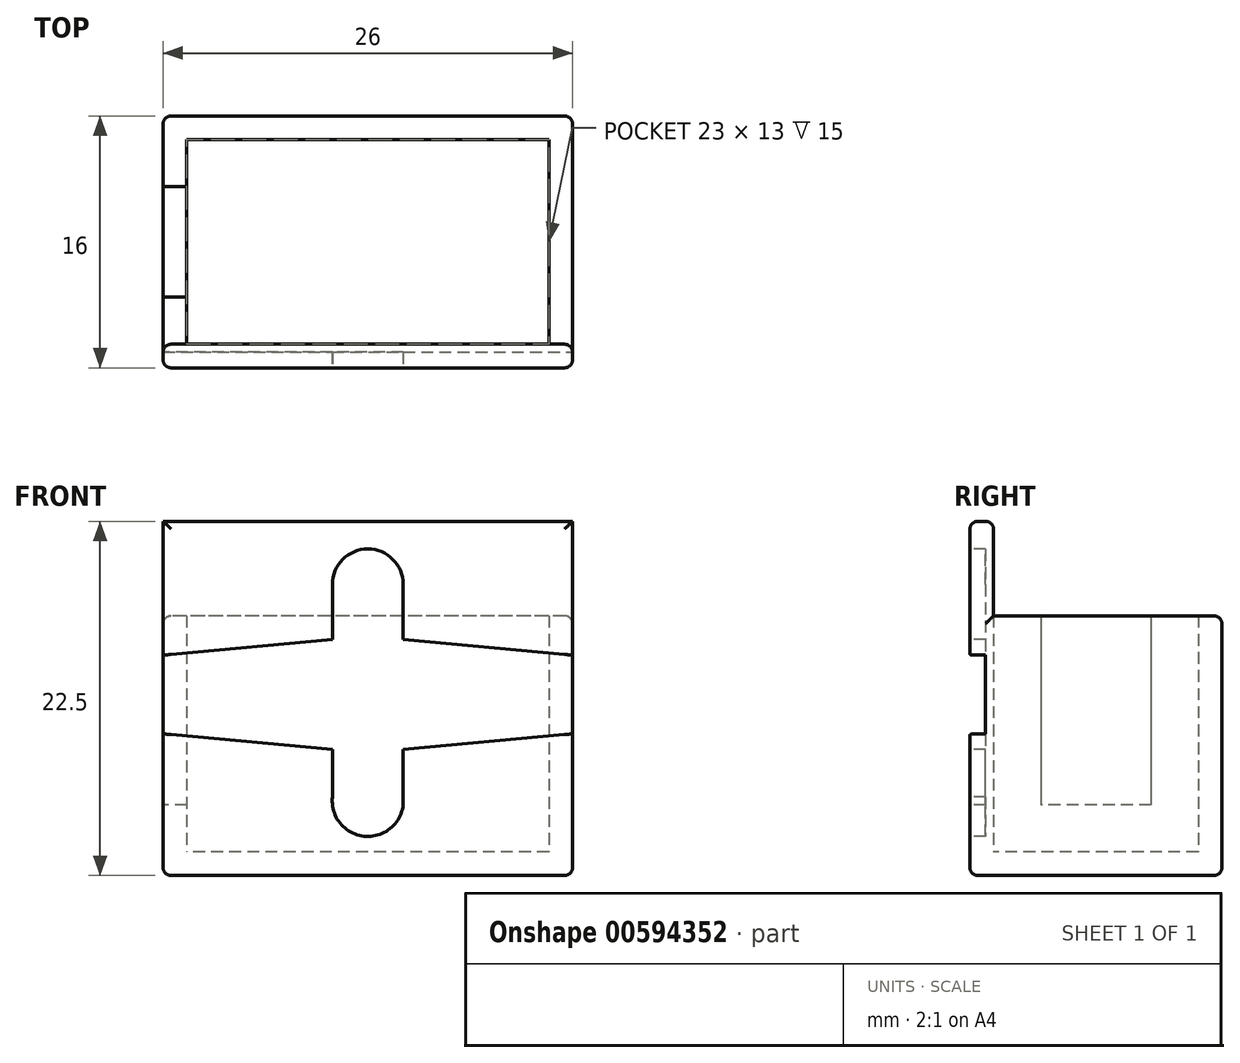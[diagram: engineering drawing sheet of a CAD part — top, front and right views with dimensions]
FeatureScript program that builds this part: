
annotation { "Feature Type Name" : "Feature", "Feature Type Description" : "" }
export const myFeature = defineFeature(function(context is Context, id is Id, definition is map)
    precondition{}
    {
        {
            var Q0;
            Q0=qCreatedBy(makeId("Top.planeOp"),FACE);
            var sketch = newSketch(context, id + "F0", { "sketchPlane" : qUnion([Q0])});
            skLineSegment(sketch, "E0.bottom", {"start": v(13, 8) * mm, "end": v(-13, 8) * mm});
            skLineSegment(sketch, "E0.top", {"start": v(13, -8) * mm, "end": v(-13, -8) * mm});
            skLineSegment(sketch, "E0.left", {"start": v(13, 8) * mm, "end": v(13, -8) * mm});
            skLineSegment(sketch, "E0.right", {"start": v(-13, 8) * mm, "end": v(-13, -8) * mm});
            skPoint(sketch, "E0.middle", {"position": v(0, 0) * mm});
            skLineSegment(sketch, "E1.bottom", {"start": v(11.5, 6.5) * mm, "end": v(-11.5, 6.5) * mm});
            skLineSegment(sketch, "E1.top", {"start": v(11.5, -6.5) * mm, "end": v(-11.5, -6.5) * mm});
            skLineSegment(sketch, "E1.left", {"start": v(11.5, 6.5) * mm, "end": v(11.5, -6.5) * mm});
            skLineSegment(sketch, "E1.right", {"start": v(-11.5, 6.5) * mm, "end": v(-11.5, -6.5) * mm});
            skLineSegment(sketch, "E2.bottom", {"start": v(-11.5, 3.5) * mm, "end": v(-13, 3.5) * mm});
            skLineSegment(sketch, "E2.top", {"start": v(-11.5, -3.5) * mm, "end": v(-13, -3.5) * mm});
            skLineSegment(sketch, "E2.left", {"start": v(-11.5, 3.5) * mm, "end": v(-11.5, -3.5) * mm});
            skLineSegment(sketch, "E2.right", {"start": v(-13, 3.5) * mm, "end": v(-13, -3.5) * mm});
            skSolve(sketch);
        }
        {
            var Q0;
            {var subQ9=sQuery(id+"F0.wireOp",EDGE,"E0.bottom");Q0=makeQuery(id+"F0.imprint","IMPRINT",FACE,{"disambiguationData":[TD([[makeQuery(id+"F0.imprint","IMPRINT",EDGE,{"derivedFrom":subQ9}),1.0]])]});}
            extrude(context, id + "F1", {"entities" : qUnion([Q0]), "depth" : 15 * mm, "offsetDistance" : 25 * mm});
        }
        {
            var Q0;
            {var subQ1=sQuery(id+"F0.wireOp",EDGE,"E1.bottom");Q0=makeQuery(id+"F0.imprint","IMPRINT",FACE,{"disambiguationData":[TD([[makeQuery(id+"F0.imprint","IMPRINT",EDGE,{"derivedFrom":subQ1}),1.0]])]});}
            var Q1;
            {var subQ9=sQuery(id+"F0.wireOp",EDGE,"E0.bottom");Q1=makeQuery(id+"F0.imprint","IMPRINT",FACE,{"disambiguationData":[TD([[makeQuery(id+"F0.imprint","IMPRINT",EDGE,{"derivedFrom":subQ9}),1.0]])]});}
            var Q2;
            Q2=makeQuery(id+"F0.imprint","IMPRINT",FACE,{"disambiguationData":[TD([[makeQuery(id+"F0.imprint","IMPRINT",EDGE,{"derivedFrom":sQuery(id+"F0.wireOp",EDGE,"E2.bottom")}),1.0]])]});
            extrude(context, id + "F2", {"entities" : qUnion([Q0, Q1, Q2]), "operationType" : NewBodyOperationType.ADD, "oppositeDirection" : true, "depth" : 1.5 * mm, "offsetDistance" : 25 * mm});
        }
        {
            var Q0;
            Q0=makeQuery(id+"F1.opExtrude","CAP_FACE",FACE,{"disambiguationData":[OSD([sQuery(id+"F0.wireOp",EDGE,"E0.bottom"),sQuery(id+"F0.wireOp",EDGE,"E0.top"),sQuery(id+"F0.wireOp",EDGE,"E0.left"),sQuery(id+"F0.wireOp",EDGE,"E0.right"),sQuery(id+"F0.wireOp",EDGE,"E1.bottom"),sQuery(id+"F0.wireOp",EDGE,"E1.top"),sQuery(id+"F0.wireOp",EDGE,"E1.left"),sQuery(id+"F0.wireOp",EDGE,"E1.right"),sQuery(id+"F0.wireOp",EDGE,"E2.bottom"),sQuery(id+"F0.wireOp",EDGE,"E2.top")])],"isStart":false});
            var sketch = newSketch(context, id + "F3", { "sketchPlane" : qUnion([Q0])});
            skLineSegment(sketch, "E3", {"start": v(-11.5, -6.5) * mm, "end": v(-13, -6.5) * mm});
            skLineSegment(sketch, "E4", {"start": v(11.5, -6.5) * mm, "end": v(13, -6.5) * mm});
            skSolve(sketch);
        }
        {
            var Q0;
            Q0 = qSketchRegion(id + "F3", true);
            var Q1;
            {var subQ4=sQuery(id+"F3.wireOp",EDGE,"E3");Q1=makeQuery(id+"F3.imprint","IMPRINT",FACE,{"disambiguationData":[TD([[makeQuery(id+"F3.imprint","IMPRINT",EDGE,{"derivedFrom":subQ4}),1.0]])]});}
            extrude(context, id + "F4", {"entities" : qUnion([Q0, Q1]), "operationType" : NewBodyOperationType.ADD, "depth" : 6 * mm, "offsetDistance" : 25 * mm});
        }
        {
            var Q0;
            Q0=makeQuery(id+"F0.imprint","IMPRINT",FACE,{"disambiguationData":[TD([[makeQuery(id+"F0.imprint","IMPRINT",EDGE,{"derivedFrom":sQuery(id+"F0.wireOp",EDGE,"E2.bottom")}),1.0]])]});
            extrude(context, id + "F5", {"entities" : qUnion([Q0]), "operationType" : NewBodyOperationType.ADD, "depth" : 3 * mm, "offsetDistance" : 25 * mm});
        }
        {
            var Q0;
            {var subQ0=sQuery(id+"F0.wireOp",EDGE,"E0.top");Q0=makeQuery(id+"F4.boolean.opBoolean","MERGE",FACE,{"derivedFrom":[makeQuery(id+"F2.boolean.opBoolean","MERGE",FACE,{"derivedFrom":[makeQuery(id+"F1.opExtrude","SWEPT_FACE",FACE,{"disambiguationData":[OSD([subQ0])]}),makeQuery(id+"F2.opExtrude","SWEPT_FACE",FACE,{"disambiguationData":[OSD([subQ0])]})]}),makeQuery(id+"F4.opExtrude","SWEPT_FACE",FACE,{"disambiguationData":[OSD([subQ0])]})]});}
            var sketch = newSketch(context, id + "F6", { "sketchPlane" : qUnion([Q0])});
            skLineSegment(sketch, "E5.bottom", {"start": v(17.25, 13.5) * mm, "end": v(-17.25, 13.5) * mm});
            skLineSegment(sketch, "E5.top", {"start": v(17.25, 6.5) * mm, "end": v(-17.25, 6.5) * mm});
            skLineSegment(sketch, "E5.left", {"start": v(17.25, 13.5) * mm, "end": v(17.25, 6.5) * mm});
            skLineSegment(sketch, "E5.right", {"start": v(-17.25, 13.5) * mm, "end": v(-17.25, 6.5) * mm});
            skPoint(sketch, "E5.middle", {"position": v(0, 10) * mm});
            skArc(sketch, "E6", {"start": v(2.25, 17) * mm, "mid": v(0, 19.24) * mm, "end": v(-2.25, 16.99) * mm});
            skArc(sketch, "E7", {"start": v(-2.25, 3.5) * mm, "mid": v(-0.25, 1) * mm, "end": v(2.25, 3) * mm});
            skLineSegment(sketch, "E8", {"start": v(-2.25, 3.5) * mm, "end": v(-2.25, 6.5) * mm});
            skLineSegment(sketch, "E9", {"start": v(2.25, 3) * mm, "end": v(2.25, 6.5) * mm});
            skLineSegment(sketch, "E10", {"start": v(-2.25, 16.99) * mm, "end": v(-2.24, 13.5) * mm});
            skLineSegment(sketch, "E11", {"start": v(2.25, 17) * mm, "end": v(2.25, 13.5) * mm});
            skPoint(sketch, "E12", {"position": v(13, 12.5) * mm});
            skPoint(sketch, "E13", {"position": v(13, 7.5) * mm});
            skPoint(sketch, "E14", {"position": v(-13, 12.5) * mm});
            skPoint(sketch, "E15", {"position": v(-13, 7.5) * mm});
            skLineSegment(sketch, "E16", {"start": v(-2.24, 13.5) * mm, "end": v(-13, 12.5) * mm});
            skLineSegment(sketch, "E17", {"start": v(-13, 7.5) * mm, "end": v(-2.25, 6.5) * mm});
            skLineSegment(sketch, "E18", {"start": v(2.25, 6.5) * mm, "end": v(13, 7.5) * mm});
            skLineSegment(sketch, "E19", {"start": v(13, 12.5) * mm, "end": v(2.25, 13.5) * mm});
            skSolve(sketch);
        }
        {
            var Q0;
            Q0=makeQuery(id+"F6.imprint","IMPRINT",FACE,{"disambiguationData":[TD([[makeQuery(id+"F6.imprint","IMPRINT",EDGE,{"derivedFrom":sQuery(id+"F6.wireOp",EDGE,"E6")}),1.0]])]});
            var Q1;
            {var subQ1=sQuery(id+"F6.wireOp",EDGE,"E16");Q1=makeQuery(id+"F6.imprint","IMPRINT",FACE,{"disambiguationData":[TD([[makeQuery(id+"F6.imprint","IMPRINT",EDGE,{"derivedFrom":subQ1}),1.0]])]});}
            var Q2;
            Q2=makeQuery(id+"F6.imprint","IMPRINT",FACE,{"disambiguationData":[TD([[makeQuery(id+"F6.imprint","IMPRINT",EDGE,{"derivedFrom":sQuery(id+"F6.wireOp",EDGE,"E7")}),1.0]])]});
            extrude(context, id + "F7", {"entities" : qUnion([Q0, Q1, Q2]), "operationType" : NewBodyOperationType.REMOVE, "oppositeDirection" : true, "depth" : 1 * mm, "offsetDistance" : 25 * mm});
        }
        {
            var Q0;
            Q0=makeQuery(id+"F1.opExtrude","CAP_EDGE",EDGE,{"disambiguationData":[OSD([sQuery(id+"F0.wireOp",EDGE,"E0.left")])],"isStart":false});
            var Q1;
            Q1=makeQuery(id+"F1.opExtrude","CAP_EDGE",EDGE,{"disambiguationData":[OSD([sQuery(id+"F0.wireOp",EDGE,"E0.bottom")])],"isStart":false});
            var Q2;
            {var subQ0=sQuery(id+"F0.wireOp",EDGE,"E0.right");Q2=makeQuery(id+"F1.opExtrude","CAP_EDGE",EDGE,{"disambiguationData":[OSD([subQ0]),TDD([makeQuery(id+"F0.imprint","IMPRINT",EDGE,{"disambiguationData":[TD([[makeQuery(id+"F0.imprint","INTERSECT",VERTEX,{"derivedFrom":[sQuery(id+"F0.wireOp",EDGE,"E0.bottom"),subQ0]}),-1.0]])],"derivedFrom":subQ0})])],"isStart":false});}
            var Q3;
            {var subQ0=sQuery(id+"F0.wireOp",EDGE,"E0.right");Q3=makeQuery(id+"F1.opExtrude","CAP_EDGE",EDGE,{"disambiguationData":[OSD([subQ0]),TDD([makeQuery(id+"F0.imprint","IMPRINT",EDGE,{"disambiguationData":[TD([[makeQuery(id+"F0.imprint","INTERSECT",VERTEX,{"derivedFrom":[sQuery(id+"F0.wireOp",EDGE,"E0.top"),subQ0]}),1.0]])],"derivedFrom":subQ0})])],"isStart":false});}
            var Q4;
            Q4=makeQuery(id+"F4.opExtrude","SWEPT_EDGE",EDGE,{"disambiguationData":[OSD([sQuery(id+"F0.wireOp",EDGE,"E0.left"),sQuery(id+"F3.wireOp",EDGE,"E4")])]});
            var Q5;
            Q5=makeQuery(id+"F4.opExtrude","CAP_EDGE",EDGE,{"disambiguationData":[OSD([sQuery(id+"F0.wireOp",EDGE,"E1.top"),sQuery(id+"F3.wireOp",EDGE,"E3"),sQuery(id+"F3.wireOp",EDGE,"E4")])],"isStart":false});
            var Q6;
            {var subQ0=sQuery(id+"F0.wireOp",EDGE,"E0.right");var subQ1=sQuery(id+"F0.wireOp",EDGE,"E0.top");Q6=makeQuery(id+"F7.boolean.opBoolean","SPLIT",EDGE,{"disambiguationData":[TD([makeQuery(id+"F7.opExtrude","SWEPT_FACE",FACE,{"disambiguationData":[OSD([sQuery(id+"F6.wireOp",EDGE,"E17")])]})])],"derivedFrom":makeQuery(id+"F4.boolean.opBoolean","MERGE",EDGE,{"derivedFrom":[makeQuery(id+"F2.boolean.opBoolean","MERGE",EDGE,{"derivedFrom":[makeQuery(id+"F1.opExtrude","SWEPT_EDGE",EDGE,{"disambiguationData":[OSD([subQ1,subQ0])]}),makeQuery(id+"F2.opExtrude","SWEPT_EDGE",EDGE,{"disambiguationData":[OSD([subQ1,subQ0])]})]}),makeQuery(id+"F4.opExtrude","SWEPT_EDGE",EDGE,{"disambiguationData":[OSD([subQ1,subQ0])]})]})});}
            var Q7;
            Q7=makeQuery(id+"F2.opExtrude","CAP_EDGE",EDGE,{"disambiguationData":[OSD([sQuery(id+"F0.wireOp",EDGE,"E0.top")])],"isStart":false});
            var Q8;
            Q8=makeQuery(id+"F2.opExtrude","CAP_EDGE",EDGE,{"disambiguationData":[OSD([sQuery(id+"F0.wireOp",EDGE,"E0.right"),sQuery(id+"F0.wireOp",EDGE,"E2.right")])],"isStart":false});
            var Q9;
            Q9=makeQuery(id+"F2.opExtrude","CAP_EDGE",EDGE,{"disambiguationData":[OSD([sQuery(id+"F0.wireOp",EDGE,"E0.left")])],"isStart":false});
            var Q10;
            Q10=makeQuery(id+"F2.opExtrude","CAP_EDGE",EDGE,{"disambiguationData":[OSD([sQuery(id+"F0.wireOp",EDGE,"E0.bottom")])],"isStart":false});
            var Q11;
            {var subQ0=sQuery(id+"F0.wireOp",EDGE,"E0.left");var subQ1=sQuery(id+"F0.wireOp",EDGE,"E0.bottom");Q11=makeQuery(id+"F2.boolean.opBoolean","MERGE",EDGE,{"derivedFrom":[makeQuery(id+"F1.opExtrude","SWEPT_EDGE",EDGE,{"disambiguationData":[OSD([subQ1,subQ0])]}),makeQuery(id+"F2.opExtrude","SWEPT_EDGE",EDGE,{"disambiguationData":[OSD([subQ1,subQ0])]})]});}
            var Q12;
            {var subQ0=sQuery(id+"F0.wireOp",EDGE,"E0.right");var subQ1=sQuery(id+"F0.wireOp",EDGE,"E0.bottom");Q12=makeQuery(id+"F2.boolean.opBoolean","MERGE",EDGE,{"derivedFrom":[makeQuery(id+"F1.opExtrude","SWEPT_EDGE",EDGE,{"disambiguationData":[OSD([subQ1,subQ0])]}),makeQuery(id+"F2.opExtrude","SWEPT_EDGE",EDGE,{"disambiguationData":[OSD([subQ1,subQ0])]})]});}
            var Q13;
            Q13=makeQuery(id+"F4.opExtrude","CAP_EDGE",EDGE,{"disambiguationData":[OSD([sQuery(id+"F0.wireOp",EDGE,"E0.top")])],"isStart":false});
            var Q14;
            {var subQ0=sQuery(id+"F0.wireOp",EDGE,"E0.top");var subQ1=sQuery(id+"F0.wireOp",EDGE,"E0.right");Q14=makeQuery(id+"F7.boolean.opBoolean","SPLIT",EDGE,{"disambiguationData":[TD([makeQuery(id+"F7.opExtrude","SWEPT_FACE",FACE,{"disambiguationData":[OSD([sQuery(id+"F6.wireOp",EDGE,"E16")])]})])],"derivedFrom":makeQuery(id+"F4.boolean.opBoolean","MERGE",EDGE,{"derivedFrom":[makeQuery(id+"F2.boolean.opBoolean","MERGE",EDGE,{"derivedFrom":[makeQuery(id+"F1.opExtrude","SWEPT_EDGE",EDGE,{"disambiguationData":[OSD([subQ0,subQ1])]}),makeQuery(id+"F2.opExtrude","SWEPT_EDGE",EDGE,{"disambiguationData":[OSD([subQ0,subQ1])]})]}),makeQuery(id+"F4.opExtrude","SWEPT_EDGE",EDGE,{"disambiguationData":[OSD([subQ0,subQ1])]})]})});}
            var Q15;
            Q15=makeQuery(id+"F4.opExtrude","SWEPT_EDGE",EDGE,{"disambiguationData":[OSD([sQuery(id+"F0.wireOp",EDGE,"E0.right"),sQuery(id+"F3.wireOp",EDGE,"E3")])]});
            var Q16;
            {var subQ0=sQuery(id+"F0.wireOp",EDGE,"E0.left");var subQ1=sQuery(id+"F0.wireOp",EDGE,"E0.top");Q16=makeQuery(id+"F7.boolean.opBoolean","SPLIT",EDGE,{"disambiguationData":[TD([makeQuery(id+"F7.opExtrude","SWEPT_FACE",FACE,{"disambiguationData":[OSD([sQuery(id+"F6.wireOp",EDGE,"E19")])]})])],"derivedFrom":makeQuery(id+"F4.boolean.opBoolean","MERGE",EDGE,{"derivedFrom":[makeQuery(id+"F2.boolean.opBoolean","MERGE",EDGE,{"derivedFrom":[makeQuery(id+"F1.opExtrude","SWEPT_EDGE",EDGE,{"disambiguationData":[OSD([subQ1,subQ0])]}),makeQuery(id+"F2.opExtrude","SWEPT_EDGE",EDGE,{"disambiguationData":[OSD([subQ1,subQ0])]})]}),makeQuery(id+"F4.opExtrude","SWEPT_EDGE",EDGE,{"disambiguationData":[OSD([subQ1,subQ0])]})]})});}
            var Q17;
            {var subQ0=sQuery(id+"F0.wireOp",EDGE,"E0.top");var subQ1=sQuery(id+"F0.wireOp",EDGE,"E0.left");Q17=makeQuery(id+"F7.boolean.opBoolean","SPLIT",EDGE,{"disambiguationData":[TD([makeQuery(id+"F7.opExtrude","SWEPT_FACE",FACE,{"disambiguationData":[OSD([sQuery(id+"F6.wireOp",EDGE,"E18")])]})])],"derivedFrom":makeQuery(id+"F4.boolean.opBoolean","MERGE",EDGE,{"derivedFrom":[makeQuery(id+"F2.boolean.opBoolean","MERGE",EDGE,{"derivedFrom":[makeQuery(id+"F1.opExtrude","SWEPT_EDGE",EDGE,{"disambiguationData":[OSD([subQ0,subQ1])]}),makeQuery(id+"F2.opExtrude","SWEPT_EDGE",EDGE,{"disambiguationData":[OSD([subQ0,subQ1])]})]}),makeQuery(id+"F4.opExtrude","SWEPT_EDGE",EDGE,{"disambiguationData":[OSD([subQ0,subQ1])]})]})});}
            fillet(context, id + "F8", {"entities" : qUnion([Q0, Q1, Q2, Q3, Q4, Q5, Q6, Q7, Q8, Q9, Q10, Q11, Q12, Q13, Q14, Q15, Q16, Q17]), "radius" : 0.5 * mm, "tangentPropagation" : true, "allowEdgeOverflow" : false});
        }
    });
